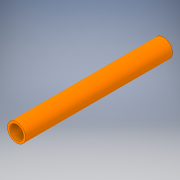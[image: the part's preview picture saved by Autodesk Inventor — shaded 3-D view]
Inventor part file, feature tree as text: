
AUTODESK INVENTOR PART (.ipt)
format: ipt  version: 2018 (Build 220112000, 112)  size: 107,520 bytes
history: native  units: in
note: dims shown in document units (in); Inventor stores cm internally (conversion verified against a paired STEP export)
features: extrude x1, sketch x1
ambient origin geometry x8: Origin, YZ Plane, XZ Plane, XY Plane, X Axis, Y Axis, Z Axis, Center Point
bodies: Solid1 (feature_tree)
feature tree (2):
  extrude  "Extrusion1"  Depth=10.584in
  sketch  "Sketch1"  dims[d0=1.315in d1=1.0in d2=10.584in d3=0.0in]
